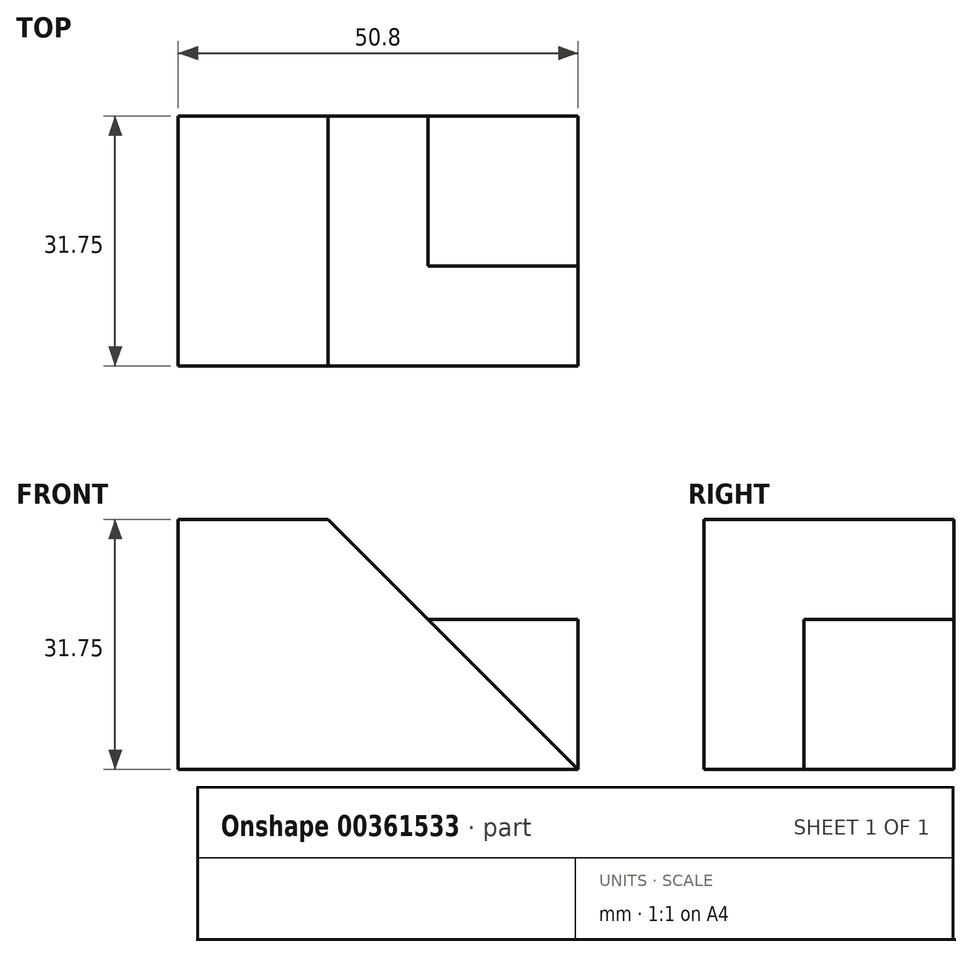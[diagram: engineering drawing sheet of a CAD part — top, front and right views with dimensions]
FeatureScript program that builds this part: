
annotation { "Feature Type Name" : "Feature", "Feature Type Description" : "" }
export const myFeature = defineFeature(function(context is Context, id is Id, definition is map)
    precondition{}
    {
        {
            var Q0;
            Q0=qCreatedBy(makeId("Front.planeOp"),FACE);
            var sketch = newSketch(context, id + "F0", { "sketchPlane" : qUnion([Q0])});
            skLineSegment(sketch, "E0", {"start": v(0, 0) * mm, "end": v(0, 31.75) * mm});
            skLineSegment(sketch, "E1", {"start": v(0, 31.75) * mm, "end": v(19.05, 31.75) * mm});
            skLineSegment(sketch, "E2", {"start": v(19.05, 31.75) * mm, "end": v(50.8, 0) * mm});
            skLineSegment(sketch, "E3", {"start": v(50.8, 0) * mm, "end": v(0, 0) * mm});
            skSolve(sketch);
        }
        {
            var Q0;
            Q0=makeQuery(id+"F0.imprint","IMPRINT",FACE,{"disambiguationData":[TD([[makeQuery(id+"F0.imprint","IMPRINT",EDGE,{"derivedFrom":sQuery(id+"F0.wireOp",EDGE,"E0")}),-1.0]])]});
            extrude(context, id + "F1", {"entities" : qUnion([Q0]), "depth" : 31.75 * mm});
        }
        {
            var Q0;
            Q0=makeQuery(id+"F1.opExtrude","CAP_FACE",FACE,{"disambiguationData":[OSD([sQuery(id+"F0.wireOp",EDGE,"E0"),sQuery(id+"F0.wireOp",EDGE,"E1"),sQuery(id+"F0.wireOp",EDGE,"E2"),sQuery(id+"F0.wireOp",EDGE,"E3")])],"isStart":true});
            var sketch = newSketch(context, id + "F2", { "sketchPlane" : qUnion([Q0])});
            skLineSegment(sketch, "E4", {"start": v(-50.8, 0) * mm, "end": v(-50.8, 19.05) * mm});
            skLineSegment(sketch, "E5", {"start": v(-50.81, 19.04) * mm, "end": v(-31.76, 19.04) * mm});
            skSolve(sketch);
        }
        {
            var Q0;
            {var subQ1=makeQuery(id+"F1.opExtrude","CAP_EDGE",EDGE,{"disambiguationData":[OSD([sQuery(id+"F0.wireOp",EDGE,"E2")])],"isStart":true});var subQ3=sQuery(id+"F2.wireOp",EDGE,"E5");var subQ5=makeQuery(id+"F2.imprint","INTERSECT",VERTEX,{"derivedFrom":[subQ1,subQ3]});Q0=makeQuery(id+"F2.imprint","IMPRINT",FACE,{"disambiguationData":[TD([[makeQuery(id+"F2.imprint","IMPRINT",EDGE,{"disambiguationData":[TD([[subQ5,1.0]])],"derivedFrom":subQ3}),-1.0]])]});}
            extrude(context, id + "F3", {"entities" : qUnion([Q0]), "oppositeDirection" : true, "depth" : 19.05 * mm});
        }
    });
